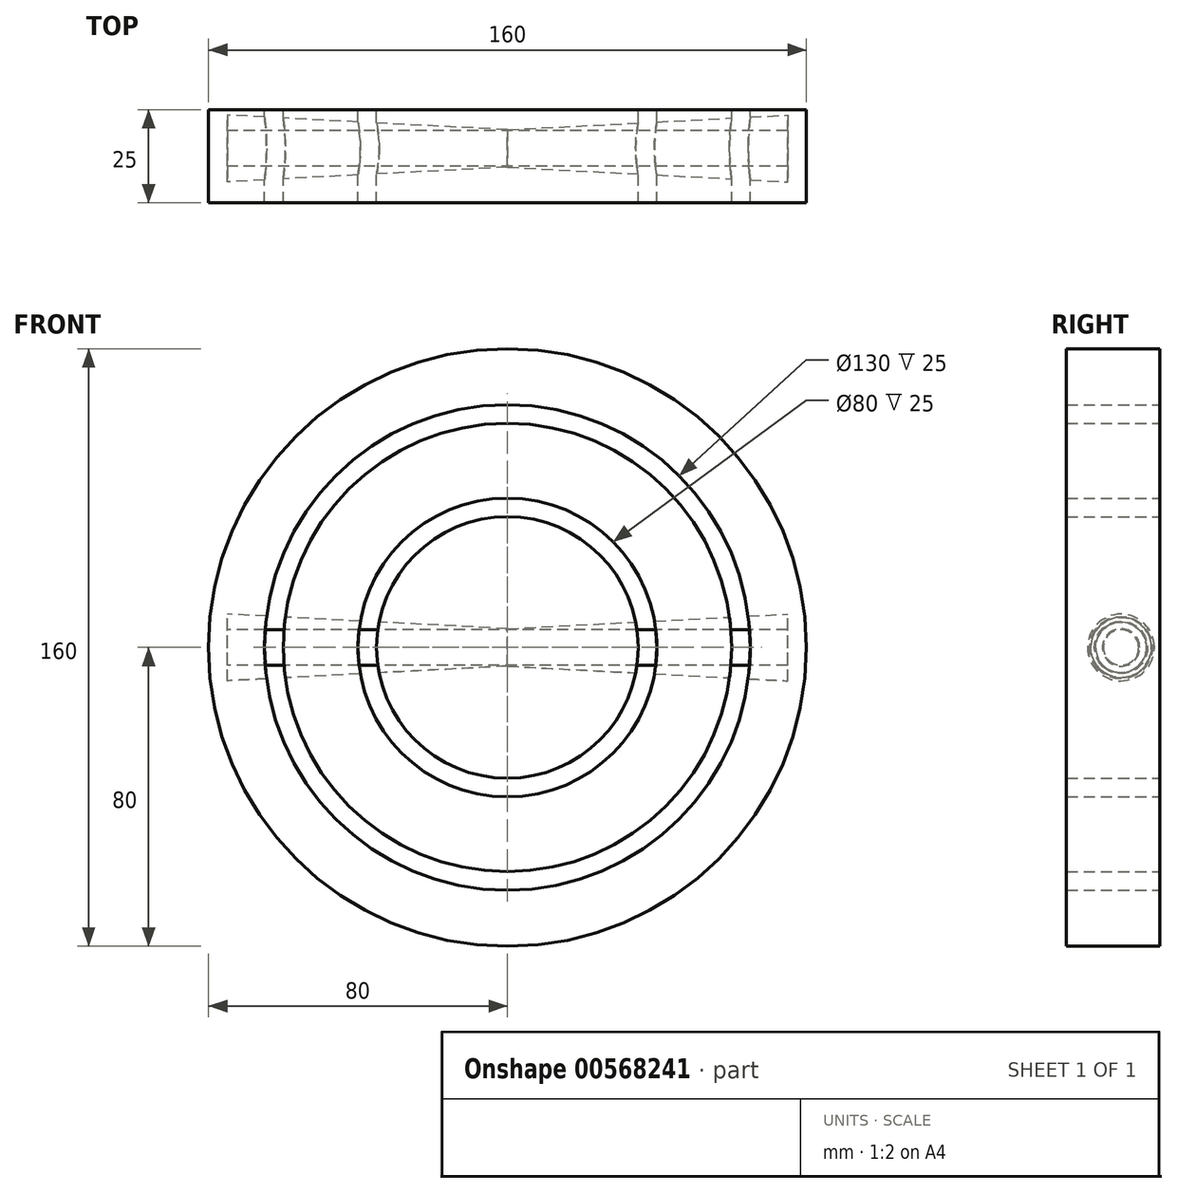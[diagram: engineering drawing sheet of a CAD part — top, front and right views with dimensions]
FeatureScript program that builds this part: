
annotation { "Feature Type Name" : "Feature", "Feature Type Description" : "" }
export const myFeature = defineFeature(function(context is Context, id is Id, definition is map)
    precondition{}
    {
        {
            var Q0;
            Q0=qCreatedBy(makeId("Front.planeOp"),FACE);
            var sketch = newSketch(context, id + "F0", { "sketchPlane" : qUnion([Q0])});
            skCircle(sketch, "E0", {"center": v(0, 0) * mm, "radius": 80 * mm});
            skCircle(sketch, "E1", {"center": v(0, 0) * mm, "radius": 65 * mm});
            skCircle(sketch, "E2", {"center": v(0, 0) * mm, "radius": 60 * mm});
            skCircle(sketch, "E3", {"center": v(0, 0) * mm, "radius": 40 * mm});
            skCircle(sketch, "E4", {"center": v(0, 0) * mm, "radius": 35 * mm});
            skSolve(sketch);
        }
        {
            var Q0;
            Q0=qCreatedBy(makeId("Right.planeOp"),FACE);
            var sketch = newSketch(context, id + "F1", { "sketchPlane" : qUnion([Q0])});
            skCircle(sketch, "E5", {"center": v(-10.41, 0) * mm, "radius": 5 * mm});
            skSolve(sketch);
        }
        {
            var Q0;
            Q0 = qSketchRegion(id + "F0", true);
            var Q1;
            Q1=makeQuery(id+"F0.imprint","IMPRINT",FACE,{"disambiguationData":[TD([[makeQuery(id+"F0.imprint","IMPRINT",EDGE,{"derivedFrom":sQuery(id+"F0.wireOp",EDGE,"E2")}),1.0]])]});
            var Q2;
            Q2=makeQuery(id+"F0.imprint","IMPRINT",FACE,{"disambiguationData":[TD([[makeQuery(id+"F0.imprint","IMPRINT",EDGE,{"derivedFrom":sQuery(id+"F0.wireOp",EDGE,"E4")}),1.0]])]});
            extrude(context, id + "F2", {"entities" : qUnion([Q0, Q1, Q2]), "depth" : 25 * mm, "offsetDistance" : 25 * mm});
        }
        {
            var Q0;
            Q0=makeQuery(id+"F1.imprint","IMPRINT",FACE,{"disambiguationData":[TD([[makeQuery(id+"F1.imprint","IMPRINT",EDGE,{"derivedFrom":sQuery(id+"F1.wireOp",EDGE,"E5")}),1.0]])]});
            extrude(context, id + "F3", {"entities" : qUnion([Q0]), "operationType" : NewBodyOperationType.REMOVE, "endBound" : BoundingType.SYMMETRIC, "depth" : 150 * mm, "offsetDistance" : 25 * mm, "hasDraft" : true, "draftAngle" : 3 * degree});
        }
        {
            var Q0;
            Q0 = qSketchRegion(id + "F1", true);
            var sketch = newSketch(context, id + "F4", { "sketchPlane" : qUnion([Q0])});
            skCircle(sketch, "E6", {"center": v(-10.41, 0) * mm, "radius": 4.75 * mm});
            skSolve(sketch);
        }
        {
            var Q0;
            Q0 = qSketchRegion(id + "F4", true);
            extrude(context, id + "F5", {"entities" : qUnion([Q0]), "operationType" : NewBodyOperationType.ADD, "endBound" : BoundingType.SYMMETRIC, "depth" : 155 * mm, "offsetDistance" : 25 * mm});
        }
    });
